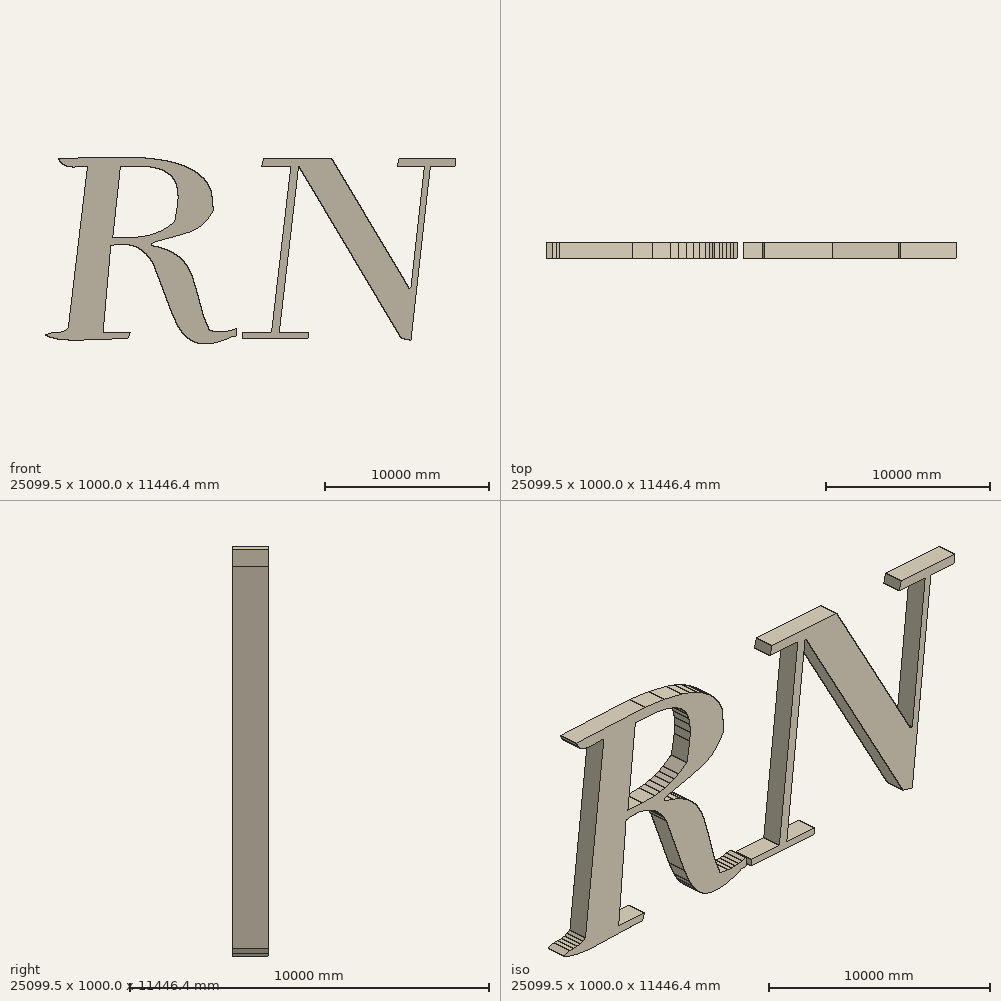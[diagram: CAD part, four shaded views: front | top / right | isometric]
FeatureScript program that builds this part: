
annotation { "Feature Type Name" : "Feature", "Feature Type Description" : "" }
export const myFeature = defineFeature(function(context is Context, id is Id, definition is map)
    precondition{}
    {
        {
            var Q0;
            Q0=qCreatedBy(makeId("Front.planeOp"),FACE);
            var sketch = newSketch(context, id + "F0", { "sketchPlane" : qUnion([Q0])});
            skPoint(sketch, "E0.0", {"position": v(-7898.75, 5700.65) * mm});
            skPoint(sketch, "E1.0", {"position": v(-7792.79, 5489.47) * mm});
            skPoint(sketch, "E2.0", {"position": v(-7646.18, 5339.69) * mm});
            skPoint(sketch, "E3.0", {"position": v(-7462.59, 5242.52) * mm});
            skPoint(sketch, "E4.0", {"position": v(-7245.8, 5188.75) * mm});
            skPoint(sketch, "E5.0", {"position": v(-6999.45, 5169.52) * mm});
            skPoint(sketch, "E6.0", {"position": v(-6727.36, 5175.5) * mm});
            skPoint(sketch, "E7.0", {"position": v(-6120.91, 5226.71) * mm});
            skPoint(sketch, "E8.0", {"position": v(-3458.32, 5783.84) * mm});
            skPoint(sketch, "E9.0", {"position": v(-2234.32, 5700.65) * mm});
            skPoint(sketch, "E10.0", {"position": v(-1107.36, 5517.85) * mm});
            skPoint(sketch, "E11.0", {"position": v(-593.57, 5380.34) * mm});
            skPoint(sketch, "E12.0", {"position": v(-119.57, 5207.24) * mm});
            skPoint(sketch, "E13.0", {"position": v(309.02, 4995.14) * mm});
            skPoint(sketch, "E14.0", {"position": v(686.95, 4740.44) * mm});
            skPoint(sketch, "E15.0", {"position": v(1009.21, 4439.72) * mm});
            skPoint(sketch, "E16.0", {"position": v(1270.2, 4089.26) * mm});
            skPoint(sketch, "E17.0", {"position": v(1465.02, 3685.63) * mm});
            skPoint(sketch, "E18.0", {"position": v(1583.55, 2500.51) * mm});
            skPoint(sketch, "E19.0", {"position": v(1345.88, 2102.02) * mm});
            skPoint(sketch, "E20.0", {"position": v(1091.24, 1787.01) * mm});
            skPoint(sketch, "E21.0", {"position": v(818.05, 1542.08) * mm});
            skPoint(sketch, "E22.0", {"position": v(524.84, 1353.6) * mm});
            skPoint(sketch, "E23.0", {"position": v(210.26, 1208.22) * mm});
            skPoint(sketch, "E24.0", {"position": v(-489.32, 992.7) * mm});
            skPoint(sketch, "E25.0", {"position": v(-1735.66, 655.48) * mm});
            skPoint(sketch, "E26.0", {"position": v(-2209.41, 485.56) * mm});
            skPoint(sketch, "E27.0", {"position": v(-2209.66, 366.66) * mm});
            skPoint(sketch, "E28.0", {"position": v(-1668.52, 242.4) * mm});
            skPoint(sketch, "E29.0", {"position": v(-1210.15, 81.39) * mm});
            skPoint(sketch, "E30.0", {"position": v(-825.75, -114.72) * mm});
            skPoint(sketch, "E31.0", {"position": v(-506.66, -343.54) * mm});
            skPoint(sketch, "E32.0", {"position": v(-244.33, -602.88) * mm});
            skPoint(sketch, "E33.0", {"position": v(-30.22, -890.72) * mm});
            skPoint(sketch, "E34.0", {"position": v(144.34, -1204.69) * mm});
            skPoint(sketch, "E35.0", {"position": v(287.78, -1542.64) * mm});
            skPoint(sketch, "E36.0", {"position": v(515.8, -2282.2) * mm});
            skPoint(sketch, "E37.0", {"position": v(-4698.92, 367.03) * mm});
            skPoint(sketch, "E38.0", {"position": v(-4223.09, 441.55) * mm});
            skPoint(sketch, "E39.0", {"position": v(-3799.14, 443.39) * mm});
            skPoint(sketch, "E40.0", {"position": v(-3422.92, 378.63) * mm});
            skPoint(sketch, "E41.0", {"position": v(-3090.03, 253.14) * mm});
            skPoint(sketch, "E42.0", {"position": v(-2796.45, 73.33) * mm});
            skPoint(sketch, "E43.0", {"position": v(-2537.9, -155.19) * mm});
            skPoint(sketch, "E44.0", {"position": v(-2310.12, -426.06) * mm});
            skPoint(sketch, "E45.0", {"position": v(-2109.2, -733.37) * mm});
            skPoint(sketch, "E46.0", {"position": v(-957.7, -3775.67) * mm});
            skPoint(sketch, "E47.0", {"position": v(-642.89, -4476.6) * mm});
            skPoint(sketch, "E48.0", {"position": v(-458.44, -4784.95) * mm});
            skPoint(sketch, "E49.0", {"position": v(-250.3, -5056.98) * mm});
            skPoint(sketch, "E50.0", {"position": v(-14.47, -5286.78) * mm});
            skPoint(sketch, "E51.0", {"position": v(253.72, -5468.24) * mm});
            skPoint(sketch, "E52.0", {"position": v(557.8, -5595.5) * mm});
            skPoint(sketch, "E53.0", {"position": v(902.4, -5662.2) * mm});
            skPoint(sketch, "E54.0", {"position": v(1291.68, -5662.51) * mm});
            skPoint(sketch, "E55.0", {"position": v(1729.67, -5590.37) * mm});
            skPoint(sketch, "E56.0", {"position": v(2220.88, -5439.67) * mm});
            skPoint(sketch, "E57.0", {"position": v(2769.22, -5204.38) * mm});
            skPoint(sketch, "E58.0", {"position": v(3006.04, -5204.38) * mm});
            skPoint(sketch, "E59.0", {"position": v(3006.04, -4731) * mm});
            skPoint(sketch, "E60.0", {"position": v(2772.15, -4805.4) * mm});
            skPoint(sketch, "E61.0", {"position": v(2546.32, -4858.68) * mm});
            skPoint(sketch, "E62.0", {"position": v(2323.42, -4891.82) * mm});
            skPoint(sketch, "E63.0", {"position": v(2097.71, -4906.1) * mm});
            skPoint(sketch, "E64.0", {"position": v(1863.46, -4903.05) * mm});
            skPoint(sketch, "E65.0", {"position": v(1346.5, -4849.16) * mm});
            skPoint(sketch, "E66.0", {"position": v(976.62, -3952.92) * mm});
            skPoint(sketch, "E67.0", {"position": v(-7306.34, -4730.8) * mm});
            skPoint(sketch, "E68.0", {"position": v(-7451.6, -4838.3) * mm});
            skPoint(sketch, "E69.0", {"position": v(-7631.41, -4912.75) * mm});
            skPoint(sketch, "E70.0", {"position": v(-7840.03, -4959.26) * mm});
            skPoint(sketch, "E71.0", {"position": v(-8071.6, -4983.07) * mm});
            skPoint(sketch, "E72.0", {"position": v(-8320.5, -4988.99) * mm});
            skPoint(sketch, "E73.0", {"position": v(-8698.55, -5113.56) * mm});
            skPoint(sketch, "E74.0", {"position": v(-8468.45, -5228.73) * mm});
            skPoint(sketch, "E75.0", {"position": v(-8168.77, -5316.01) * mm});
            skPoint(sketch, "E76.0", {"position": v(-7811.47, -5378.58) * mm});
            skPoint(sketch, "E77.0", {"position": v(-6969.8, -5441.5) * mm});
            skPoint(sketch, "E78.0", {"position": v(-3632.27, -5322.97) * mm});
            skPoint(sketch, "E79.0", {"position": v(-3513.86, -4967.87) * mm});
            skPoint(sketch, "E80.0", {"position": v(-5173.16, -4967.56) * mm});
            skPoint(sketch, "E81.0", {"position": v(-4580.5, 840.79) * mm});
            skPoint(sketch, "E82.0", {"position": v(-3628.36, 834.8) * mm});
            skPoint(sketch, "E83.0", {"position": v(-2837.47, 898.52) * mm});
            skPoint(sketch, "E84.0", {"position": v(-2490.42, 958.89) * mm});
            skPoint(sketch, "E85.0", {"position": v(-2169.38, 1039.88) * mm});
            skPoint(sketch, "E86.0", {"position": v(-1869.45, 1142.3) * mm});
            skPoint(sketch, "E87.0", {"position": v(-1586.12, 1267.42) * mm});
            skPoint(sketch, "E88.0", {"position": v(-1314.27, 1416.16) * mm});
            skPoint(sketch, "E89.0", {"position": v(-786.69, 1788.78) * mm});
            skPoint(sketch, "E90.0", {"position": v(-607.85, 2851.04) * mm});
            skPoint(sketch, "E91.0", {"position": v(-581.73, 3300.5) * mm});
            skPoint(sketch, "E92.0", {"position": v(-602.24, 3698.2) * mm});
            skPoint(sketch, "E93.0", {"position": v(-672.67, 4046.17) * mm});
            skPoint(sketch, "E94.0", {"position": v(-796.45, 4345.6) * mm});
            skPoint(sketch, "E95.0", {"position": v(-976.75, 4599.02) * mm});
            skPoint(sketch, "E96.0", {"position": v(-1217.23, 4807.7) * mm});
            skPoint(sketch, "E97.0", {"position": v(-1520.82, 4973.66) * mm});
            skPoint(sketch, "E98.0", {"position": v(-1891.3, 5098.78) * mm});
            skPoint(sketch, "E99.0", {"position": v(-2331.6, 5184.9) * mm});
            skPoint(sketch, "E100.0", {"position": v(-2845.28, 5233.67) * mm});
            skPoint(sketch, "E101.0", {"position": v(-4106.39, 5226.71) * mm});
            skPoint(sketch, "E102.0", {"position": v(4666.2, 5700.65) * mm});
            skPoint(sketch, "E103.0", {"position": v(4547.79, 5227.02) * mm});
            skPoint(sketch, "E104.0", {"position": v(6325.74, 5226.71) * mm});
            skPoint(sketch, "E105.0", {"position": v(5140.07, -4967.87) * mm});
            skPoint(sketch, "E106.0", {"position": v(3362.24, -4967.87) * mm});
            skPoint(sketch, "E107.0", {"position": v(3362.24, -5322.97) * mm});
            skPoint(sketch, "E108.0", {"position": v(7392.03, -5322.97) * mm});
            skPoint(sketch, "E109.0", {"position": v(7392.03, -4967.87) * mm});
            skPoint(sketch, "E110.0", {"position": v(5613.83, -4967.56) * mm});
            skPoint(sketch, "E111.0", {"position": v(6799.86, 5226.95) * mm});
            skPoint(sketch, "E112.0", {"position": v(8814.51, 5700.65) * mm});
            skPoint(sketch, "E113.0", {"position": v(13082.33, -5322.97) * mm});
            skPoint(sketch, "E114.0", {"position": v(13674.62, -5441.38) * mm});
            skPoint(sketch, "E115.0", {"position": v(14866.95, 5226.89) * mm});
            skPoint(sketch, "E116.0", {"position": v(16400.94, 5226.89) * mm});
            skPoint(sketch, "E117.0", {"position": v(16400.94, 5700.65) * mm});
            skPoint(sketch, "E118.0", {"position": v(12963.8, 5700.65) * mm});
            skPoint(sketch, "E119.0", {"position": v(12845.52, 5227.02) * mm});
            skPoint(sketch, "E120.0", {"position": v(14504.94, 5226.71) * mm});
            skPoint(sketch, "E121.0", {"position": v(13674.86, -2241.55) * mm});
            skPoint(sketch, "E122.0", {"position": v(13556.09, -2241.43) * mm});
            skLineSegment(sketch, "E123", {"start": v(-7898.75, 5700.65) * mm, "end": v(-3458.32, 5783.84) * mm});
            skLineSegment(sketch, "E124", {"start": v(-3458.32, 5783.84) * mm, "end": v(-2234.32, 5700.65) * mm});
            skLineSegment(sketch, "E125", {"start": v(-2234.32, 5700.65) * mm, "end": v(-1107.36, 5517.85) * mm});
            skLineSegment(sketch, "E126", {"start": v(-1107.36, 5517.85) * mm, "end": v(-593.57, 5380.34) * mm});
            skLineSegment(sketch, "E127", {"start": v(-593.57, 5380.34) * mm, "end": v(-119.57, 5207.24) * mm});
            skLineSegment(sketch, "E128", {"start": v(-119.57, 5207.24) * mm, "end": v(309.02, 4995.14) * mm});
            skLineSegment(sketch, "E129", {"start": v(309.02, 4995.14) * mm, "end": v(686.95, 4740.44) * mm});
            skLineSegment(sketch, "E130", {"start": v(686.95, 4740.44) * mm, "end": v(1009.21, 4439.72) * mm});
            skLineSegment(sketch, "E131", {"start": v(1009.21, 4439.72) * mm, "end": v(1270.2, 4089.26) * mm});
            skLineSegment(sketch, "E132", {"start": v(1270.2, 4089.26) * mm, "end": v(1465.02, 3685.63) * mm});
            skLineSegment(sketch, "E133", {"start": v(1465.02, 3685.63) * mm, "end": v(1583.55, 2500.51) * mm});
            skLineSegment(sketch, "E134", {"start": v(1583.55, 2500.51) * mm, "end": v(1345.88, 2102.02) * mm});
            skLineSegment(sketch, "E135", {"start": v(1345.88, 2102.02) * mm, "end": v(1091.24, 1787.01) * mm});
            skLineSegment(sketch, "E136", {"start": v(1091.24, 1787.01) * mm, "end": v(818.05, 1542.08) * mm});
            skLineSegment(sketch, "E137", {"start": v(818.05, 1542.08) * mm, "end": v(524.84, 1353.6) * mm});
            skLineSegment(sketch, "E138", {"start": v(524.84, 1353.6) * mm, "end": v(210.26, 1208.22) * mm});
            skLineSegment(sketch, "E139", {"start": v(210.26, 1208.22) * mm, "end": v(-489.32, 992.7) * mm});
            skLineSegment(sketch, "E140", {"start": v(-489.32, 992.7) * mm, "end": v(-1735.66, 655.48) * mm});
            skLineSegment(sketch, "E141", {"start": v(-1735.66, 655.48) * mm, "end": v(-2209.41, 485.56) * mm});
            skLineSegment(sketch, "E142", {"start": v(-2209.41, 485.56) * mm, "end": v(-2209.66, 366.66) * mm});
            skLineSegment(sketch, "E143", {"start": v(-2209.66, 366.66) * mm, "end": v(-1668.52, 242.4) * mm});
            skLineSegment(sketch, "E144", {"start": v(-1668.52, 242.4) * mm, "end": v(-1210.15, 81.39) * mm});
            skLineSegment(sketch, "E145", {"start": v(-1210.15, 81.39) * mm, "end": v(-825.75, -114.72) * mm});
            skLineSegment(sketch, "E146", {"start": v(-825.75, -114.72) * mm, "end": v(-506.66, -343.54) * mm});
            skLineSegment(sketch, "E147", {"start": v(-506.66, -343.54) * mm, "end": v(-244.33, -602.88) * mm});
            skLineSegment(sketch, "E148", {"start": v(-244.33, -602.88) * mm, "end": v(-30.22, -890.72) * mm});
            skLineSegment(sketch, "E149", {"start": v(-30.22, -890.72) * mm, "end": v(144.34, -1204.69) * mm});
            skLineSegment(sketch, "E150", {"start": v(144.34, -1204.69) * mm, "end": v(287.78, -1542.64) * mm});
            skLineSegment(sketch, "E151", {"start": v(287.78, -1542.64) * mm, "end": v(515.8, -2282.2) * mm});
            skLineSegment(sketch, "E152", {"start": v(515.8, -2282.2) * mm, "end": v(976.62, -3952.92) * mm});
            skLineSegment(sketch, "E153", {"start": v(976.62, -3952.92) * mm, "end": v(1346.5, -4849.16) * mm});
            skLineSegment(sketch, "E154", {"start": v(1346.5, -4849.16) * mm, "end": v(1863.46, -4903.05) * mm});
            skLineSegment(sketch, "E155", {"start": v(1863.46, -4903.05) * mm, "end": v(2097.71, -4906.1) * mm});
            skLineSegment(sketch, "E156", {"start": v(2097.71, -4906.1) * mm, "end": v(2323.42, -4891.82) * mm});
            skLineSegment(sketch, "E157", {"start": v(2323.42, -4891.82) * mm, "end": v(2546.32, -4858.68) * mm});
            skLineSegment(sketch, "E158", {"start": v(2546.32, -4858.68) * mm, "end": v(2772.15, -4805.4) * mm});
            skLineSegment(sketch, "E159", {"start": v(3006.04, -5204.38) * mm, "end": v(2769.22, -5204.38) * mm});
            skLineSegment(sketch, "E160", {"start": v(2769.22, -5204.38) * mm, "end": v(2220.88, -5439.67) * mm});
            skLineSegment(sketch, "E161", {"start": v(2220.88, -5439.67) * mm, "end": v(1729.67, -5590.37) * mm});
            skLineSegment(sketch, "E162", {"start": v(1729.67, -5590.37) * mm, "end": v(1291.68, -5662.51) * mm});
            skLineSegment(sketch, "E163", {"start": v(1291.68, -5662.51) * mm, "end": v(902.4, -5662.2) * mm});
            skLineSegment(sketch, "E164", {"start": v(902.4, -5662.2) * mm, "end": v(557.8, -5595.5) * mm});
            skLineSegment(sketch, "E165", {"start": v(557.8, -5595.5) * mm, "end": v(253.72, -5468.24) * mm});
            skLineSegment(sketch, "E166", {"start": v(253.72, -5468.24) * mm, "end": v(-14.47, -5286.78) * mm});
            skLineSegment(sketch, "E167", {"start": v(-14.47, -5286.78) * mm, "end": v(-250.3, -5056.98) * mm});
            skLineSegment(sketch, "E168", {"start": v(-250.3, -5056.98) * mm, "end": v(-458.44, -4784.95) * mm});
            skLineSegment(sketch, "E169", {"start": v(-458.44, -4784.95) * mm, "end": v(-642.89, -4476.6) * mm});
            skLineSegment(sketch, "E170", {"start": v(-642.89, -4476.6) * mm, "end": v(-957.7, -3775.67) * mm});
            skLineSegment(sketch, "E171", {"start": v(-957.7, -3775.67) * mm, "end": v(-2109.2, -733.37) * mm});
            skLineSegment(sketch, "E172", {"start": v(-2109.2, -733.37) * mm, "end": v(-2310.12, -426.06) * mm});
            skLineSegment(sketch, "E173", {"start": v(-2310.12, -426.06) * mm, "end": v(-2537.9, -155.19) * mm});
            skLineSegment(sketch, "E174", {"start": v(-2537.9, -155.19) * mm, "end": v(-2796.45, 73.33) * mm});
            skLineSegment(sketch, "E175", {"start": v(-2796.45, 73.33) * mm, "end": v(-3090.03, 253.14) * mm});
            skLineSegment(sketch, "E176", {"start": v(-3090.03, 253.14) * mm, "end": v(-3422.92, 378.63) * mm});
            skLineSegment(sketch, "E177", {"start": v(-3422.92, 378.63) * mm, "end": v(-3799.14, 443.39) * mm});
            skLineSegment(sketch, "E178", {"start": v(-3799.14, 443.39) * mm, "end": v(-4223.09, 441.55) * mm});
            skLineSegment(sketch, "E179", {"start": v(-4223.09, 441.55) * mm, "end": v(-4698.92, 367.03) * mm});
            skLineSegment(sketch, "E180", {"start": v(-4698.92, 367.03) * mm, "end": v(-5173.16, -4967.56) * mm});
            skLineSegment(sketch, "E181", {"start": v(-5173.16, -4967.56) * mm, "end": v(-3513.86, -4967.87) * mm});
            skLineSegment(sketch, "E182", {"start": v(-3513.86, -4967.87) * mm, "end": v(-3632.27, -5322.97) * mm});
            skLineSegment(sketch, "E183", {"start": v(-3632.27, -5322.97) * mm, "end": v(-6969.8, -5441.5) * mm});
            skLineSegment(sketch, "E184", {"start": v(-6969.8, -5441.5) * mm, "end": v(-7811.47, -5378.58) * mm});
            skLineSegment(sketch, "E185", {"start": v(-7811.47, -5378.58) * mm, "end": v(-8168.77, -5316.01) * mm});
            skLineSegment(sketch, "E186", {"start": v(-8168.77, -5316.01) * mm, "end": v(-8468.45, -5228.73) * mm});
            skLineSegment(sketch, "E187", {"start": v(-8468.45, -5228.73) * mm, "end": v(-8698.55, -5113.56) * mm});
            skLineSegment(sketch, "E188", {"start": v(-8698.55, -5113.56) * mm, "end": v(-8320.5, -4988.99) * mm});
            skLineSegment(sketch, "E189", {"start": v(-8320.5, -4988.99) * mm, "end": v(-8071.6, -4983.07) * mm});
            skLineSegment(sketch, "E190", {"start": v(-8071.6, -4983.07) * mm, "end": v(-7840.03, -4959.26) * mm});
            skLineSegment(sketch, "E191", {"start": v(-7840.03, -4959.26) * mm, "end": v(-7631.41, -4912.75) * mm});
            skLineSegment(sketch, "E192", {"start": v(-7631.41, -4912.75) * mm, "end": v(-7451.6, -4838.3) * mm});
            skLineSegment(sketch, "E193", {"start": v(-7451.6, -4838.3) * mm, "end": v(-7306.34, -4730.8) * mm});
            skLineSegment(sketch, "E194", {"start": v(-7306.34, -4730.8) * mm, "end": v(-6120.91, 5226.71) * mm});
            skLineSegment(sketch, "E195", {"start": v(-6120.91, 5226.71) * mm, "end": v(-6727.36, 5175.5) * mm});
            skLineSegment(sketch, "E196", {"start": v(-6727.36, 5175.5) * mm, "end": v(-6999.45, 5169.52) * mm});
            skLineSegment(sketch, "E197", {"start": v(-6999.45, 5169.52) * mm, "end": v(-7245.8, 5188.75) * mm});
            skLineSegment(sketch, "E198", {"start": v(-7245.8, 5188.75) * mm, "end": v(-7462.59, 5242.52) * mm});
            skLineSegment(sketch, "E199", {"start": v(-7462.59, 5242.52) * mm, "end": v(-7646.18, 5339.69) * mm});
            skLineSegment(sketch, "E200", {"start": v(-7646.18, 5339.69) * mm, "end": v(-7792.79, 5489.47) * mm});
            skLineSegment(sketch, "E201", {"start": v(-7792.79, 5489.47) * mm, "end": v(-7898.75, 5700.65) * mm});
            skLineSegment(sketch, "E202", {"start": v(-4106.39, 5226.71) * mm, "end": v(-4580.5, 840.79) * mm});
            skLineSegment(sketch, "E203", {"start": v(-4580.5, 840.79) * mm, "end": v(-3628.36, 834.8) * mm});
            skLineSegment(sketch, "E204", {"start": v(-3628.36, 834.8) * mm, "end": v(-2837.47, 898.52) * mm});
            skLineSegment(sketch, "E205", {"start": v(-2837.47, 898.52) * mm, "end": v(-2490.42, 958.89) * mm});
            skLineSegment(sketch, "E206", {"start": v(-2490.42, 958.89) * mm, "end": v(-2169.38, 1039.88) * mm});
            skLineSegment(sketch, "E207", {"start": v(-2169.38, 1039.88) * mm, "end": v(-1869.45, 1142.3) * mm});
            skLineSegment(sketch, "E208", {"start": v(-1869.45, 1142.3) * mm, "end": v(-1586.12, 1267.42) * mm});
            skLineSegment(sketch, "E209", {"start": v(-1586.12, 1267.42) * mm, "end": v(-1314.27, 1416.16) * mm});
            skLineSegment(sketch, "E210", {"start": v(-1314.27, 1416.16) * mm, "end": v(-786.69, 1788.78) * mm});
            skLineSegment(sketch, "E211", {"start": v(-786.69, 1788.78) * mm, "end": v(-607.85, 2851.04) * mm});
            skLineSegment(sketch, "E212", {"start": v(-607.85, 2851.04) * mm, "end": v(-581.73, 3300.5) * mm});
            skLineSegment(sketch, "E213", {"start": v(-581.73, 3300.5) * mm, "end": v(-602.24, 3698.2) * mm});
            skLineSegment(sketch, "E214", {"start": v(-602.24, 3698.2) * mm, "end": v(-672.67, 4046.17) * mm});
            skLineSegment(sketch, "E215", {"start": v(-672.67, 4046.17) * mm, "end": v(-796.45, 4345.6) * mm});
            skLineSegment(sketch, "E216", {"start": v(-796.45, 4345.6) * mm, "end": v(-976.75, 4599.02) * mm});
            skLineSegment(sketch, "E217", {"start": v(-4106.39, 5226.71) * mm, "end": v(-2845.28, 5233.67) * mm});
            skLineSegment(sketch, "E218", {"start": v(-2845.28, 5233.67) * mm, "end": v(-2331.6, 5184.9) * mm});
            skLineSegment(sketch, "E219", {"start": v(-2331.6, 5184.9) * mm, "end": v(-1891.3, 5098.78) * mm});
            skLineSegment(sketch, "E220", {"start": v(-1891.3, 5098.78) * mm, "end": v(-1520.82, 4973.66) * mm});
            skLineSegment(sketch, "E221", {"start": v(-1520.82, 4973.66) * mm, "end": v(-1217.23, 4807.7) * mm});
            skLineSegment(sketch, "E222", {"start": v(-1217.23, 4807.7) * mm, "end": v(-976.75, 4599.02) * mm});
            skLineSegment(sketch, "E223", {"start": v(4666.2, 5700.65) * mm, "end": v(8814.51, 5700.65) * mm});
            skLineSegment(sketch, "E224", {"start": v(4666.2, 5700.65) * mm, "end": v(4547.79, 5227.02) * mm});
            skLineSegment(sketch, "E225", {"start": v(4547.79, 5227.02) * mm, "end": v(6325.74, 5226.71) * mm});
            skLineSegment(sketch, "E226", {"start": v(3006.04, -5204.38) * mm, "end": v(3006.04, -4731) * mm});
            skLineSegment(sketch, "E227", {"start": v(2772.15, -4805.4) * mm, "end": v(3006.04, -4731) * mm});
            skLineSegment(sketch, "E228", {"start": v(5140.07, -4967.87) * mm, "end": v(3362.24, -4967.87) * mm});
            skLineSegment(sketch, "E229", {"start": v(3362.24, -4967.87) * mm, "end": v(3362.24, -5322.97) * mm});
            skLineSegment(sketch, "E230", {"start": v(3362.24, -5322.97) * mm, "end": v(7392.03, -5322.97) * mm});
            skLineSegment(sketch, "E231", {"start": v(7392.03, -5322.97) * mm, "end": v(7392.03, -4967.87) * mm});
            skLineSegment(sketch, "E232", {"start": v(6325.74, 5226.71) * mm, "end": v(5140.07, -4967.87) * mm});
            skLineSegment(sketch, "E233", {"start": v(7392.03, -4967.87) * mm, "end": v(5613.83, -4967.56) * mm});
            skLineSegment(sketch, "E234", {"start": v(5613.83, -4967.56) * mm, "end": v(6799.86, 5226.95) * mm});
            skLineSegment(sketch, "E235", {"start": v(6799.86, 5226.95) * mm, "end": v(13082.33, -5322.97) * mm});
            skLineSegment(sketch, "E236", {"start": v(13082.33, -5322.97) * mm, "end": v(13674.62, -5441.38) * mm});
            skLineSegment(sketch, "E237", {"start": v(8814.51, 5700.65) * mm, "end": v(13556.09, -2241.43) * mm});
            skLineSegment(sketch, "E238", {"start": v(13556.09, -2241.43) * mm, "end": v(13674.86, -2241.55) * mm});
            skLineSegment(sketch, "E239", {"start": v(13674.86, -2241.55) * mm, "end": v(14504.94, 5226.71) * mm});
            skLineSegment(sketch, "E240", {"start": v(14504.94, 5226.71) * mm, "end": v(12845.52, 5227.02) * mm});
            skLineSegment(sketch, "E241", {"start": v(12845.52, 5227.02) * mm, "end": v(12963.8, 5700.65) * mm});
            skLineSegment(sketch, "E242", {"start": v(12963.8, 5700.65) * mm, "end": v(16400.94, 5700.65) * mm});
            skLineSegment(sketch, "E243", {"start": v(16400.94, 5700.65) * mm, "end": v(16400.94, 5226.89) * mm});
            skLineSegment(sketch, "E244", {"start": v(14866.95, 5226.89) * mm, "end": v(13674.62, -5441.38) * mm});
            skLineSegment(sketch, "E245", {"start": v(14866.95, 5226.89) * mm, "end": v(16400.94, 5226.89) * mm});
            skSolve(sketch);
        }
        {
            var Q0;
            Q0=makeQuery(id+"F0.imprint","IMPRINT",FACE,{"disambiguationData":[TD([[makeQuery(id+"F0.imprint","IMPRINT",EDGE,{"derivedFrom":sQuery(id+"F0.wireOp",EDGE,"E123")}),-1.0]])]});
            var Q1;
            Q1=makeQuery(id+"F0.imprint","IMPRINT",FACE,{"disambiguationData":[TD([[makeQuery(id+"F0.imprint","IMPRINT",EDGE,{"derivedFrom":sQuery(id+"F0.wireOp",EDGE,"E223")}),-1.0]])]});
            extrude(context, id + "F1", {"entities" : qUnion([Q0, Q1]), "depth" : 1000 * mm});
        }
    });
